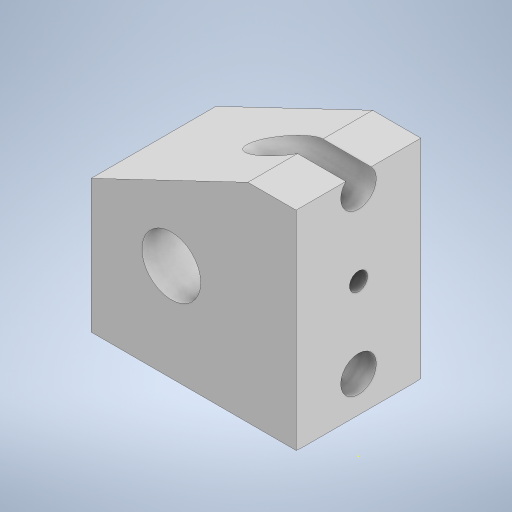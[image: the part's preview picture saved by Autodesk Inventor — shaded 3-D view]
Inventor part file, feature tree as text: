
AUTODESK INVENTOR PART (.ipt)
format: ipt  version: 2024 (Build 280153000, 153)  size: 242,176 bytes
history: native  units: in
note: dims shown in document units (in); Inventor stores cm internally (conversion verified against a paired STEP export)
features: other x3, sketch x3, extrude x1
ambient origin geometry x8: Origin, YZ Plane, XZ Plane, XY Plane, X Axis, Y Axis, Z Axis, Center Point
bodies: Body1 (feature_tree)
feature tree (7):
  other  "lower.ipt"
  extrude  "Extrusion1"  Depth=0.04in
  sketch  "Sketch2"  dims[d2=0.04in d3=0.0in]
  sketch  "Sketch3"
  other  "Solid12::lower.ipt"
  other  "TaggingFeature1"
  sketch  "Sketch1"  dims[d0=0.3937in d1=0.04in]
